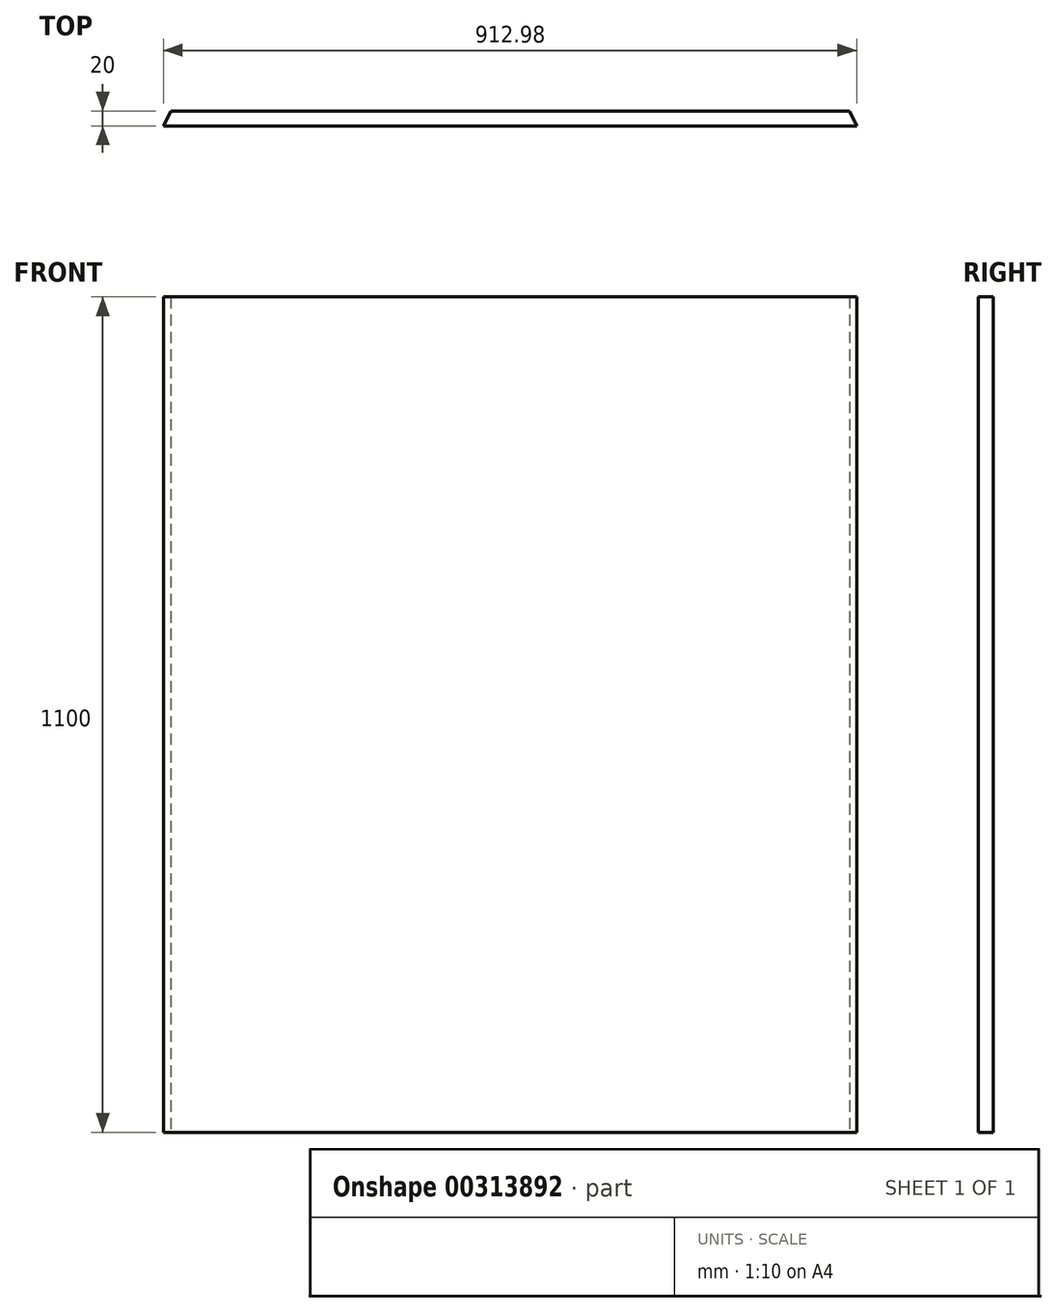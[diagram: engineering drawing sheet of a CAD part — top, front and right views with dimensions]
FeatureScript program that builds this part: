
annotation { "Feature Type Name" : "Feature", "Feature Type Description" : "" }
export const myFeature = defineFeature(function(context is Context, id is Id, definition is map)
    precondition{}
    {
        {
            var Q0;
            Q0=qCreatedBy(makeId("Top.planeOp"),FACE);
            var sketch = newSketch(context, id + "F0", { "sketchPlane" : qUnion([Q0])});
            skLineSegment(sketch, "E0.3", {"start": v(439.14, -10.04) * mm, "end": v(-473.84, -10.04) * mm});
            skLineSegment(sketch, "E1.5", {"start": v(429.5, 9.96) * mm, "end": v(-464.2, 9.96) * mm});
            skLineSegment(sketch, "E2", {"start": v(-473.84, -10.04) * mm, "end": v(-464.2, 9.96) * mm});
            skLineSegment(sketch, "E3", {"start": v(439.14, -10.04) * mm, "end": v(429.5, 9.96) * mm});
            skSolve(sketch);
        }
        {
            var Q0;
            Q0=makeQuery(id+"F0.imprint","IMPRINT",FACE,{"disambiguationData":[TD([[makeQuery(id+"F0.imprint","IMPRINT",EDGE,{"derivedFrom":sQuery(id+"F0.wireOp",EDGE,"E0.3")}),-1.0]])]});
            extrude(context, id + "F1", {"entities" : qUnion([Q0]), "depth" : 1100 * mm});
        }
    });
